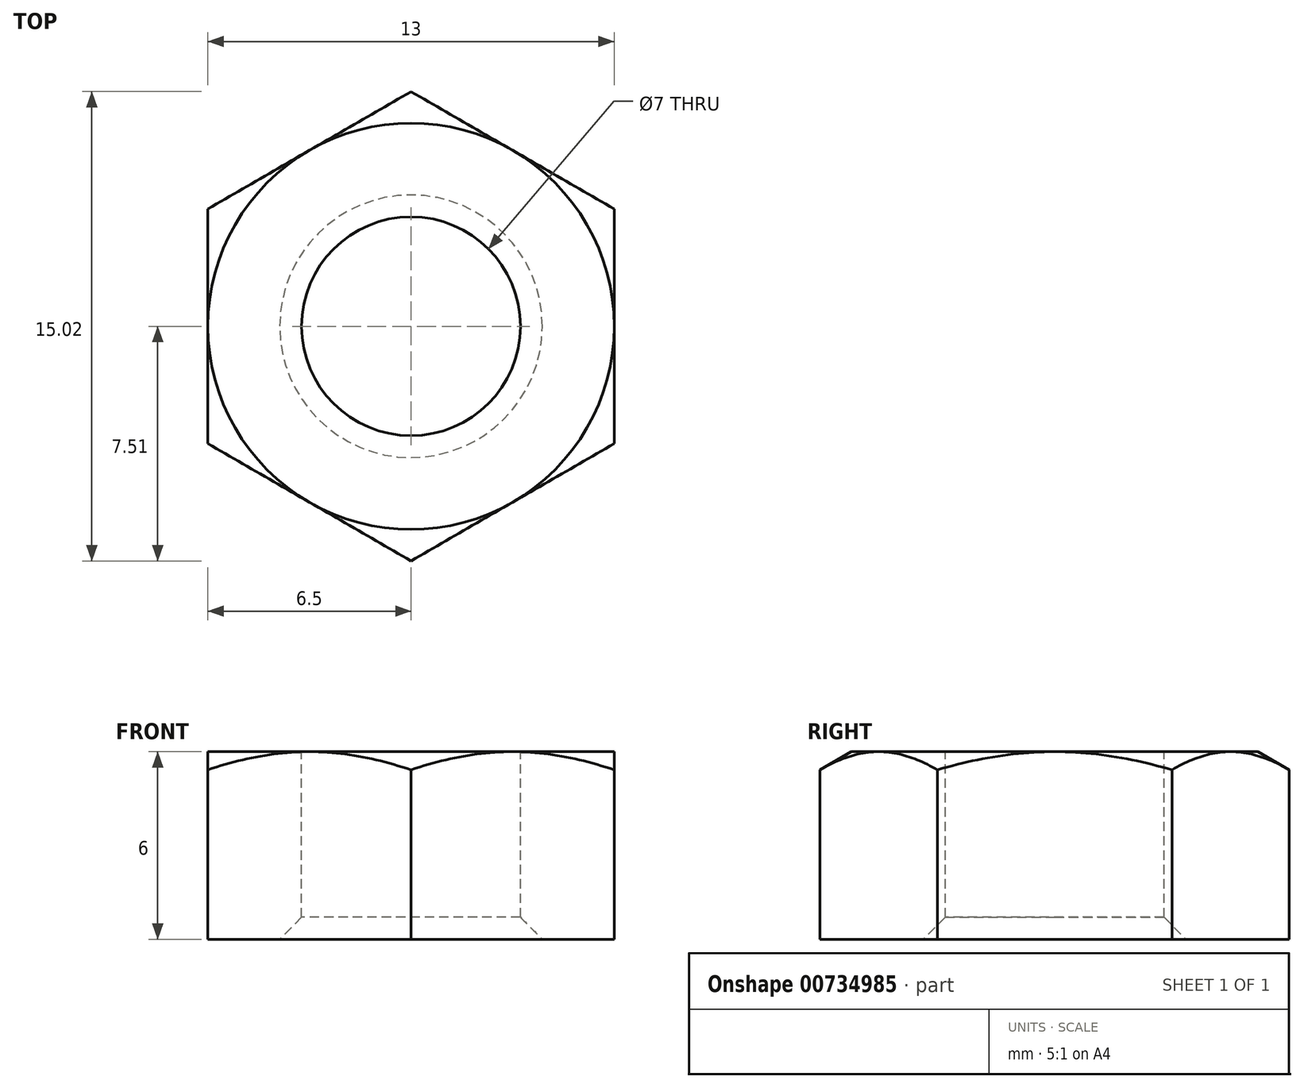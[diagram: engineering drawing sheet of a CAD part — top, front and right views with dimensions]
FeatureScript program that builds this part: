
annotation { "Feature Type Name" : "Feature", "Feature Type Description" : "" }
export const myFeature = defineFeature(function(context is Context, id is Id, definition is map)
    precondition{}
    {
        {
            var Q0;
            Q0=qCreatedBy(makeId("Top.planeOp"),FACE);
            var sketch = newSketch(context, id + "F0", { "sketchPlane" : qUnion([Q0])});
            skCircle(sketch, "E0.cCircle", {"center": v(0, 0) * mm, "radius": 6.5 * mm, "construction": true});
            skLineSegment(sketch, "E0.0", {"start": v(6.5, 3.75) * mm, "end": v(6.5, -3.75) * mm});
            skLineSegment(sketch, "E0.1", {"start": v(6.5, -3.75) * mm, "end": v(0, -7.5) * mm});
            skLineSegment(sketch, "E0.2", {"start": v(0, -7.5) * mm, "end": v(-6.5, -3.75) * mm});
            skLineSegment(sketch, "E0.3", {"start": v(-6.5, -3.75) * mm, "end": v(-6.5, 3.75) * mm});
            skLineSegment(sketch, "E0.4", {"start": v(-6.5, 3.75) * mm, "end": v(0, 7.5) * mm});
            skLineSegment(sketch, "E0.5", {"start": v(0, 7.5) * mm, "end": v(6.5, 3.75) * mm});
            skPoint(sketch, "E0.0.midPoint", {"position": v(6.5, 0) * mm});
            skSolve(sketch);
        }
        {
            var Q0;
            Q0 = qSketchRegion(id + "F0", true);
            extrude(context, id + "F1", {"entities" : qUnion([Q0]), "depth" : 6 * mm, "offsetDistance" : 25 * mm});
        }
        {
            var Q0;
            Q0=makeQuery(id+"F1.opExtrude","CAP_FACE",FACE,{"disambiguationData":[OSD([sQuery(id+"F0.wireOp",EDGE,"E0.0"),sQuery(id+"F0.wireOp",EDGE,"E0.1"),sQuery(id+"F0.wireOp",EDGE,"E0.2"),sQuery(id+"F0.wireOp",EDGE,"E0.3"),sQuery(id+"F0.wireOp",EDGE,"E0.4"),sQuery(id+"F0.wireOp",EDGE,"E0.5")])],"isStart":false});
            var sketch = newSketch(context, id + "F2", { "sketchPlane" : qUnion([Q0])});
            skCircle(sketch, "E1", {"center": v(0, 0) * mm, "radius": 3.5 * mm});
            skSolve(sketch);
        }
        {
            var Q0;
            Q0 = qSketchRegion(id + "F2", true);
            extrude(context, id + "F3", {"entities" : qUnion([Q0]), "operationType" : NewBodyOperationType.REMOVE, "endBound" : BoundingType.THROUGH_ALL, "oppositeDirection" : true, "depth" : 25 * mm, "offsetDistance" : 25 * mm});
        }
        {
            var Q0;
            Q0=qCreatedBy(makeId("Front.planeOp"),FACE);
            var sketch = newSketch(context, id + "F4", { "sketchPlane" : qUnion([Q0])});
            skLineSegment(sketch, "E2", {"start": v(6.5, 6) * mm, "end": v(10.7, 6) * mm});
            skLineSegment(sketch, "E3", {"start": v(10.7, 6) * mm, "end": v(10.7, 3.57) * mm});
            skLineSegment(sketch, "E4", {"start": v(10.7, 3.57) * mm, "end": v(6.5, 6) * mm});
            skLineSegment(sketch, "E5", {"start": v(0, 0) * mm, "end": v(0, 4.65) * mm, "construction": true});
            skSolve(sketch);
        }
        {
            var Q0;
            Q0 = qSketchRegion(id + "F4", true);
            var Q1;
            Q1=sQuery(id+"F4.wireOp",EDGE,"E5");
            revolve(context, id + "F5", {"operationType" : NewBodyOperationType.REMOVE, "surfaceOperationType" : NewSurfaceOperationType.NEW, "entities" : qUnion([Q0]), "axis" : qUnion([Q1]), "revolveType" : RevolveType.FULL, "oppositeDirection" : true});
        }
        {
            var Q0;
            Q0=makeQuery(id+"F3.boolean.opBoolean","COPY",EDGE,{"derivedFrom":makeQuery(id+"F3.opExtrude","CAP_EDGE",EDGE,{"disambiguationData":[OSD([sQuery(id+"F2.wireOp",EDGE,"E1")])],"isStart":true})});
            var Q1;
            Q1=makeQuery(id+"F3.boolean.opBoolean","INTERSECT",EDGE,{"derivedFrom":[makeQuery(id+"F1.opExtrude","CAP_FACE",FACE,{"disambiguationData":[OSD([sQuery(id+"F0.wireOp",EDGE,"E0.0"),sQuery(id+"F0.wireOp",EDGE,"E0.1"),sQuery(id+"F0.wireOp",EDGE,"E0.2"),sQuery(id+"F0.wireOp",EDGE,"E0.3"),sQuery(id+"F0.wireOp",EDGE,"E0.4"),sQuery(id+"F0.wireOp",EDGE,"E0.5")])],"isStart":true}),makeQuery(id+"F3.opExtrude","SWEPT_FACE",FACE,{"disambiguationData":[OSD([sQuery(id+"F2.wireOp",EDGE,"E1")])]})]});
            chamfer(context, id + "F6", {"entities" : qUnion([Q0, Q1]), "width" : 0.7 * mm, "tangentPropagation" : true});
        }
    });
